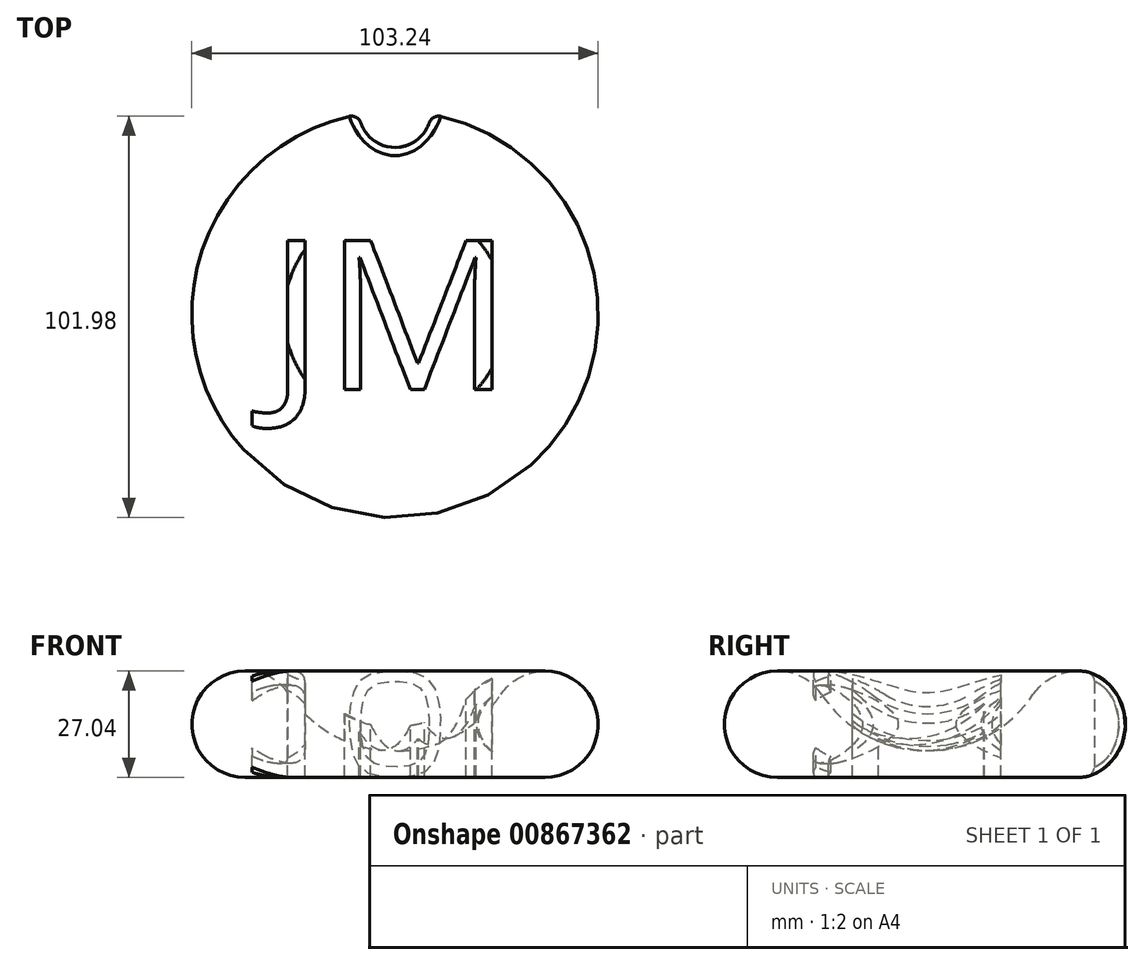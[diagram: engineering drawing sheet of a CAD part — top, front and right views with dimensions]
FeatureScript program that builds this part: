
annotation { "Feature Type Name" : "Feature", "Feature Type Description" : "" }
export const myFeature = defineFeature(function(context is Context, id is Id, definition is map)
    precondition{}
    {
        {
            var Q0;
            Q0=qCreatedBy(makeId("Front.planeOp"),FACE);
            var sketch = newSketch(context, id + "F0", { "sketchPlane" : qUnion([Q0])});
            skArc(sketch, "E0", {"start": v(-26.87, 21.05) * mm, "mid": v(-15.23, 10.52) * mm, "end": v(0, 6.7) * mm});
            skArc(sketch, "E1", {"start": v(-26.87, 21.05) * mm, "mid": v(-50.03, 19.89) * mm, "end": v(-38.1, 0) * mm});
            skLineSegment(sketch, "E2", {"start": v(0, 6.7) * mm, "end": v(0, 0) * mm});
            skLineSegment(sketch, "E3", {"start": v(0, 0) * mm, "end": v(-38.1, 0) * mm});
            skSolve(sketch);
        }
        {
            var Q0;
            Q0=makeQuery(id+"F0.imprint","IMPRINT",FACE,{"disambiguationData":[TD([[makeQuery(id+"F0.imprint","IMPRINT",EDGE,{"derivedFrom":sQuery(id+"F0.wireOp",EDGE,"E0")}),-1.0]])]});
            var Q1;
            Q1=sQuery(id+"F0.wireOp",EDGE,"E2");
            revolve(context, id + "F1", {"surfaceOperationType" : NewSurfaceOperationType.NEW, "entities" : qUnion([Q0]), "axis" : qUnion([Q1]), "revolveType" : RevolveType.FULL});
        }
        {
            var Q0;
            Q0=qCreatedBy(makeId("Top.planeOp"),FACE);
            cPlane(context, id + "F2", {"entities" : qUnion([Q0]), "cplaneType" : CPlaneType.OFFSET, "offset" : 50.8 * mm, "width" : 152.4 * mm, "height" : 152.4 * mm});
        }
        {
            var Q0;
            Q0=qCreatedBy(id+"F2.planeOp",FACE);
            var sketch = newSketch(context, id + "F3", { "sketchPlane" : qUnion([Q0])});
            skText(sketch, "E4", { "text": "JM\n", "fontName": "OpenSans-Regular.ttf"});
            const initialGuessF3  = {"E4": [-0.03215, -0.01905, 1, 0, 0.0381]};
            skSetInitialGuess(sketch, initialGuessF3);
            skSolve(sketch);
        }
        {
            var Q0;
            Q0=qSketchRegion(id+"F3",true);
            extrude(context, id + "F4", {"entities" : qUnion([Q0]), "operationType" : NewBodyOperationType.REMOVE, "oppositeDirection" : true, "depth" : 76.2 * mm, "offsetDistance" : 25.4 * mm});
        }
        {
            var Q0;
            Q0=qCreatedBy(makeId("Front.planeOp"),FACE);
            var sketch = newSketch(context, id + "F5", { "sketchPlane" : qUnion([Q0])});
            skCircle(sketch, "E5", {"center": v(-38.1, 13.52) * mm, "radius": 9.92 * mm});
            skSolve(sketch);
        }
        {
            var Q0;
            Q0=qSketchRegion(id+"F5",true);
            var Q1;
            Q1=sQuery(id+"F0.wireOp",EDGE,"E2");
            revolve(context, id + "F6", {"operationType" : NewBodyOperationType.ADD, "surfaceOperationType" : NewSurfaceOperationType.NEW, "entities" : qUnion([Q0]), "axis" : qUnion([Q1]), "revolveType" : RevolveType.FULL});
        }
        {
            var Q0;
            Q0=qCreatedBy(makeId("Top.planeOp"),FACE);
            var sketch = newSketch(context, id + "F7", { "sketchPlane" : qUnion([Q0])});
            skCircle(sketch, "E6", {"center": v(0, 51.55) * mm, "radius": 9.15 * mm});
            skSolve(sketch);
        }
        {
            var Q0;
            Q0=qSketchRegion(id+"F7",true);
            extrude(context, id + "F8", {"entities" : qUnion([Q0]), "operationType" : NewBodyOperationType.REMOVE, "depth" : 30.23 * mm, "offsetDistance" : 25.4 * mm});
        }
        {
            var Q0;
            Q0=makeQuery(id+"F8.boolean.opBoolean","INTERSECT",EDGE,{"derivedFrom":[makeQuery(id+"F1.opRevolve","SWEPT_FACE",FACE,{"disambiguationData":[OSD([sQuery(id+"F0.wireOp",EDGE,"E1")])]}),makeQuery(id+"F8.opExtrude","SWEPT_FACE",FACE,{"disambiguationData":[OSD([sQuery(id+"F7.wireOp",EDGE,"E6")])]})]});
            fillet(context, id + "F9", {"entities" : qUnion([Q0]), "radius" : 2.54 * mm, "tangentPropagation" : true, "allowEdgeOverflow" : false});
        }
    });
